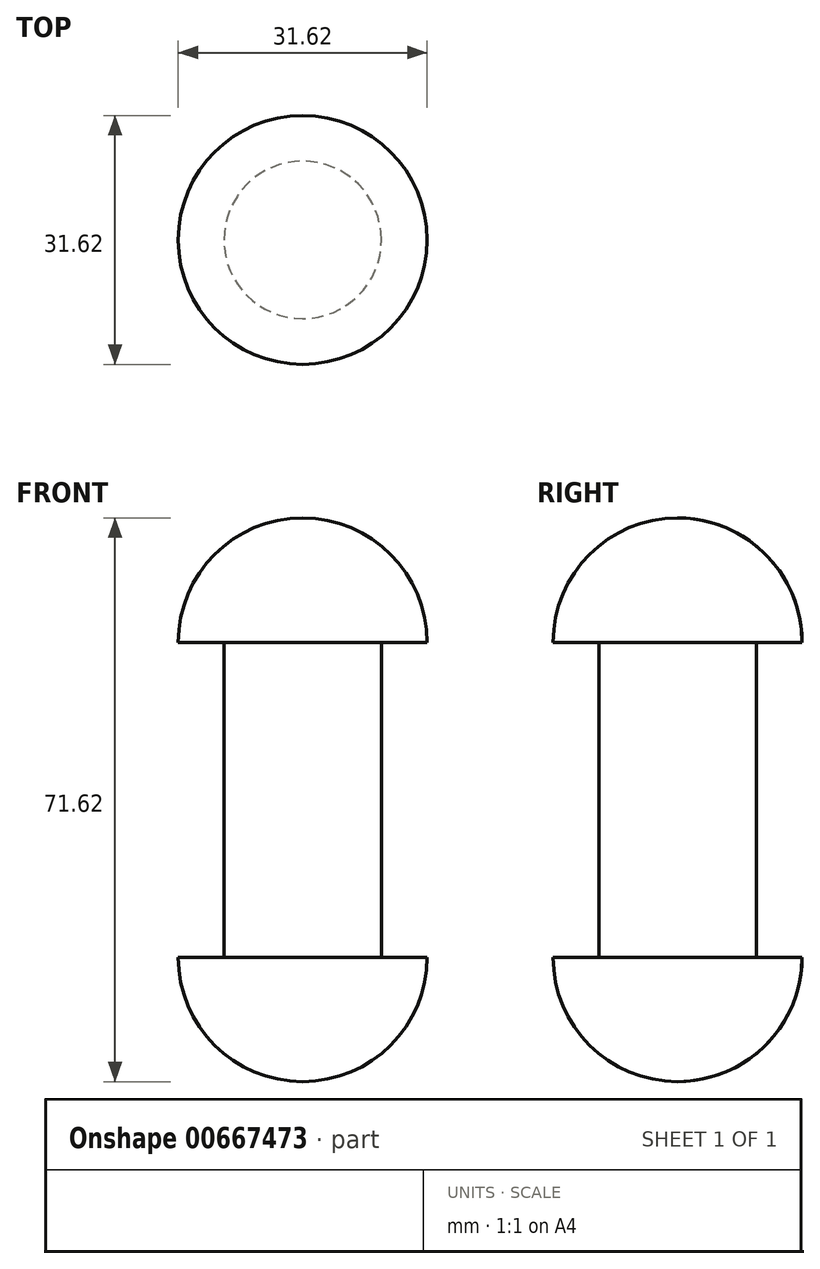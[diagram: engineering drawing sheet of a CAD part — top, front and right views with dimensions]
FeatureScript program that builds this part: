
annotation { "Feature Type Name" : "Feature", "Feature Type Description" : "" }
export const myFeature = defineFeature(function(context is Context, id is Id, definition is map)
    precondition{}
    {
        {
            var Q0;
            Q0=qCreatedBy(makeId("Top.planeOp"),FACE);
            var sketch = newSketch(context, id + "F0", { "sketchPlane" : qUnion([Q0])});
            skCircle(sketch, "E0", {"center": v(0, 0) * mm, "radius": 10 * mm});
            skSolve(sketch);
        }
        {
            var Q0;
            Q0=makeQuery(id+"F0.imprint","IMPRINT",FACE,{"disambiguationData":[TD([[makeQuery(id+"F0.imprint","IMPRINT",EDGE,{"derivedFrom":sQuery(id+"F0.wireOp",EDGE,"E0")}),1.0]])]});
            extrude(context, id + "F1", {"entities" : qUnion([Q0]), "endBound" : BoundingType.SYMMETRIC, "depth" : 40 * mm, "offsetDistance" : 25 * mm});
        }
        {
            var Q0;
            Q0=qCreatedBy(makeId("Right.planeOp"),FACE);
            var sketch = newSketch(context, id + "F2", { "sketchPlane" : qUnion([Q0])});
            skLineSegment(sketch, "E1", {"start": v(0, -20) * mm, "end": v(15.8, -20) * mm});
            skArc(sketch, "E2", {"start": v(15.8, -20) * mm, "mid": v(11.18, -31.18) * mm, "end": v(0, -35.8) * mm});
            skLineSegment(sketch, "E3", {"start": v(0, -20) * mm, "end": v(0, -35.8) * mm});
            skSolve(sketch);
        }
        {
            var Q0;
            Q0=makeQuery(id+"F2.imprint","IMPRINT",FACE,{"disambiguationData":[TD([[makeQuery(id+"F2.imprint","IMPRINT",EDGE,{"derivedFrom":sQuery(id+"F2.wireOp",EDGE,"E1")}),-1.0]])]});
            var Q1;
            Q1=sQuery(id+"F2.wireOp",EDGE,"E3");
            revolve(context, id + "F3", {"operationType" : NewBodyOperationType.ADD, "entities" : qUnion([Q0]), "axis" : qUnion([Q1]), "revolveType" : RevolveType.FULL});
        }
        {
            var Q0;
            Q0=makeQuery(id+"F1.opExtrude","SWEPT_BODY",BODY,{"disambiguationData":[OSD([sQuery(id+"F0.wireOp",EDGE,"E0")])]});
            var Q1;
            Q1=qCreatedBy(makeId("Top.planeOp"),FACE);
            mirror(context, id + "F4", {"operationType" : NewBodyOperationType.ADD, "entities" : qUnion([Q0]), "mirrorPlane" : qUnion([Q1])});
        }
    });
